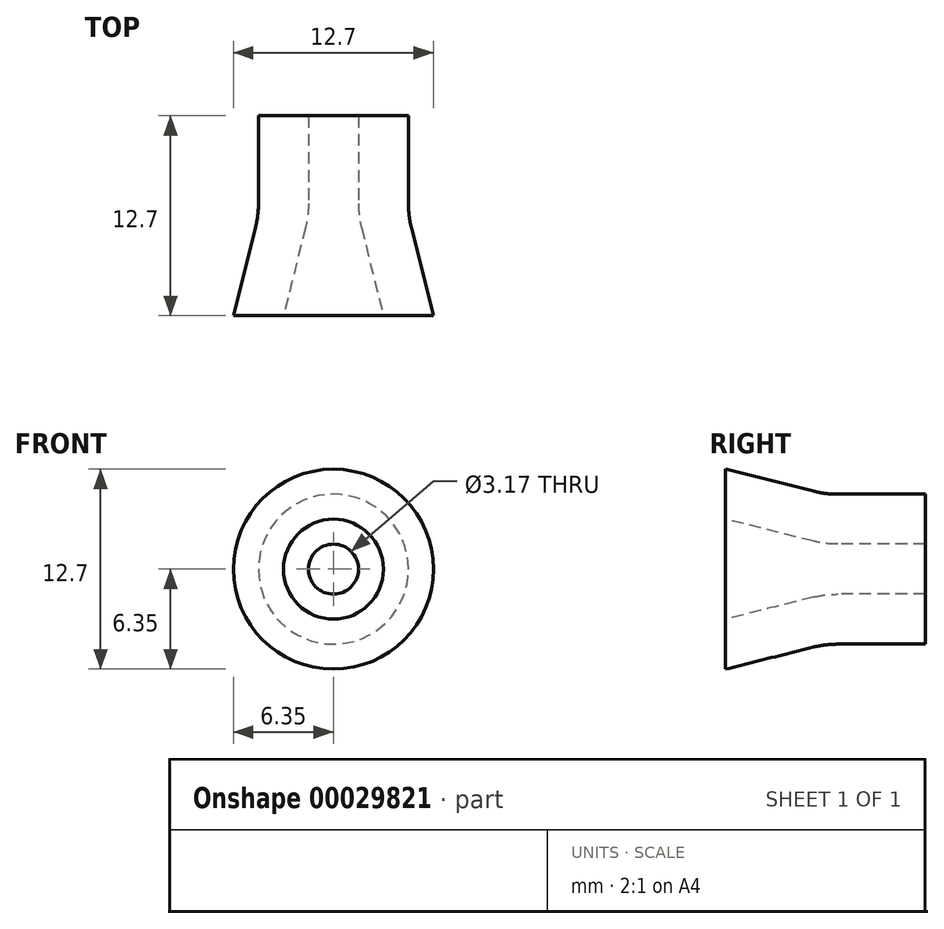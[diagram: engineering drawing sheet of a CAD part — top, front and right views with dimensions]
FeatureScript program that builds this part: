
annotation { "Feature Type Name" : "Feature", "Feature Type Description" : "" }
export const myFeature = defineFeature(function(context is Context, id is Id, definition is map)
    precondition{}
    {
        {
            var Q0;
            Q0=qCreatedBy(makeId("Top.planeOp"),FACE);
            var sketch = newSketch(context, id + "F0", { "sketchPlane" : qUnion([Q0])});
            skLineSegment(sketch, "E0", {"start": v(0, 0) * mm, "end": v(0, 41.42) * mm});
            skLineSegment(sketch, "E1", {"start": v(-1.78, 5.6) * mm, "end": v(-3.17, 0) * mm});
            skLineSegment(sketch, "E2", {"start": v(-3.18, 0) * mm, "end": v(-6.35, 0) * mm});
            skLineSegment(sketch, "E3", {"start": v(-6.35, 0) * mm, "end": v(-4.95, 5.6) * mm});
            skLineSegment(sketch, "E4", {"start": v(-4.76, 7.13) * mm, "end": v(-4.76, 12.7) * mm});
            skLineSegment(sketch, "E5", {"start": v(-4.76, 12.7) * mm, "end": v(-1.59, 12.7) * mm});
            skLineSegment(sketch, "E6", {"start": v(-1.59, 12.7) * mm, "end": v(-1.59, 7.13) * mm});
            skPoint(sketch, "E7.visualSharp", {"position": v(-1.59, 6.35) * mm});
            skArc(sketch, "E7.filletArc", {"start": v(-1.78, 5.6) * mm, "mid": v(-1.64, 6.36) * mm, "end": v(-1.59, 7.13) * mm});
            skPoint(sketch, "E8.visualSharp", {"position": v(-4.76, 6.35) * mm});
            skArc(sketch, "E8.filletArc", {"start": v(-4.95, 5.6) * mm, "mid": v(-4.81, 6.36) * mm, "end": v(-4.76, 7.13) * mm});
            skLineSegment(sketch, "E9", {"start": v(-4.76, 6.35) * mm, "end": v(-1.59, 6.35) * mm});
            skSolve(sketch);
        }
        {
            var Q0;
            {var subQ2=sQuery(id+"F0.wireOp",EDGE,"E1");Q0=makeQuery(id+"F0.imprint","IMPRINT",FACE,{"disambiguationData":[TD([[makeQuery(id+"F0.imprint","IMPRINT",EDGE,{"derivedFrom":subQ2}),-1.0]])]});}
            var Q1;
            Q1=sQuery(id+"F0.wireOp",EDGE,"E0");
            revolve(context, id + "F1", {"entities" : qUnion([Q0]), "axis" : qUnion([Q1]), "revolveType" : RevolveType.FULL});
        }
    });
